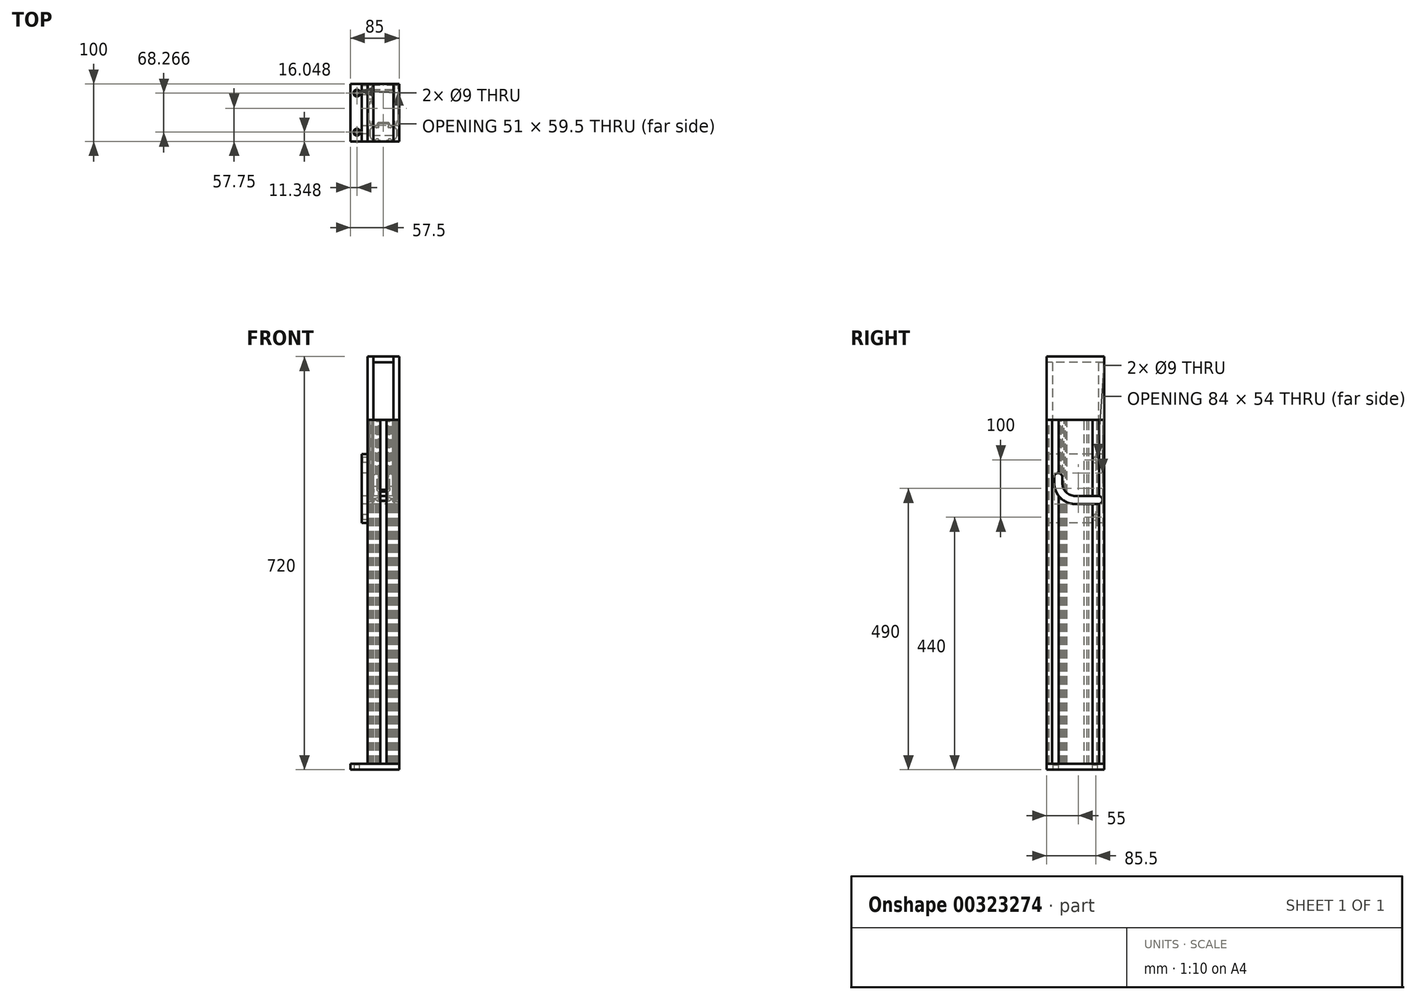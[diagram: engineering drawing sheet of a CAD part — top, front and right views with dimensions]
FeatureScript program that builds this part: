
annotation { "Feature Type Name" : "Feature", "Feature Type Description" : "" }
export const myFeature = defineFeature(function(context is Context, id is Id, definition is map)
    precondition{}
    {
        {
            var Q0;
            Q0=qCreatedBy(makeId("Top.planeOp"),FACE);
            var sketch = newSketch(context, id + "F0", { "sketchPlane" : qUnion([Q0])});
            skArc(sketch, "E0.0.0", {"start": v(6.5, -48) * mm, "mid": v(5.5, -49) * mm, "end": v(6.5, -50) * mm});
            skLineSegment(sketch, "E0.0.1", {"start": v(6.5, -50) * mm, "end": v(25.5, -50) * mm});
            skArc(sketch, "E0.0.2", {"start": v(25.5, -50) * mm, "mid": v(26.91, -49.41) * mm, "end": v(27.5, -48) * mm});
            skLineSegment(sketch, "E0.0.3", {"start": v(27.5, -48) * mm, "end": v(27.5, -41.5) * mm});
            skArc(sketch, "E0.0.4", {"start": v(27.5, -41.5) * mm, "mid": v(27.2, -40.8) * mm, "end": v(26.5, -40.5) * mm});
            skLineSegment(sketch, "E0.0.5", {"start": v(26.5, -40.5) * mm, "end": v(25.3, -40.5) * mm});
            skArc(sketch, "E0.0.6", {"start": v(25.3, -40.5) * mm, "mid": v(24.96, -40.35) * mm, "end": v(24.8, -40) * mm});
            skLineSegment(sketch, "E0.0.7", {"start": v(24.8, -40) * mm, "end": v(24.8, -30) * mm});
            skArc(sketch, "E0.0.8", {"start": v(24.8, -30) * mm, "mid": v(24.96, -29.65) * mm, "end": v(25.3, -29.5) * mm});
            skLineSegment(sketch, "E0.0.9", {"start": v(25.3, -29.5) * mm, "end": v(26.5, -29.5) * mm});
            skArc(sketch, "E0.0.10", {"start": v(26.5, -29.5) * mm, "mid": v(27.2, -29.2) * mm, "end": v(27.5, -28.5) * mm});
            skLineSegment(sketch, "E0.0.11", {"start": v(27.5, -28.5) * mm, "end": v(27.5, 29) * mm});
            skArc(sketch, "E0.0.12", {"start": v(27.5, 29) * mm, "mid": v(26.5, 30) * mm, "end": v(25.5, 29) * mm});
            skLineSegment(sketch, "E0.0.13", {"start": v(25.5, 29) * mm, "end": v(25.5, 24) * mm});
            skArc(sketch, "E0.0.14", {"start": v(25.5, 24) * mm, "mid": v(25.35, 23.65) * mm, "end": v(25, 23.5) * mm});
            skLineSegment(sketch, "E0.0.15", {"start": v(25, 23.5) * mm, "end": v(20.5, 23.5) * mm});
            skArc(sketch, "E0.0.16", {"start": v(20.5, 23.5) * mm, "mid": v(20.15, 23.65) * mm, "end": v(20, 24) * mm});
            skLineSegment(sketch, "E0.0.17", {"start": v(20, 24) * mm, "end": v(20, 47.5) * mm});
            skArc(sketch, "E0.0.18", {"start": v(20, 47.5) * mm, "mid": v(20.15, 47.85) * mm, "end": v(20.5, 48) * mm});
            skLineSegment(sketch, "E0.0.19", {"start": v(20.5, 48) * mm, "end": v(25, 48) * mm});
            skArc(sketch, "E0.0.20", {"start": v(25, 48) * mm, "mid": v(25.35, 47.85) * mm, "end": v(25.5, 47.5) * mm});
            skLineSegment(sketch, "E0.0.21", {"start": v(25.5, 47.5) * mm, "end": v(25.5, 42) * mm});
            skArc(sketch, "E0.0.22", {"start": v(25.5, 42) * mm, "mid": v(26.5, 41) * mm, "end": v(27.5, 42) * mm});
            skLineSegment(sketch, "E0.0.23", {"start": v(27.5, 42) * mm, "end": v(27.5, 48) * mm});
            skArc(sketch, "E0.0.24", {"start": v(27.5, 48) * mm, "mid": v(26.91, 49.41) * mm, "end": v(25.5, 50) * mm});
            skLineSegment(sketch, "E0.0.25", {"start": v(25.5, 50) * mm, "end": v(7, 50) * mm});
            skArc(sketch, "E0.0.26", {"start": v(7, 50) * mm, "mid": v(6, 49) * mm, "end": v(7, 48) * mm});
            skLineSegment(sketch, "E0.0.27", {"start": v(7, 48) * mm, "end": v(17.5, 48) * mm});
            skArc(sketch, "E0.0.28", {"start": v(17.5, 48) * mm, "mid": v(17.85, 47.85) * mm, "end": v(18, 47.5) * mm});
            skLineSegment(sketch, "E0.0.29", {"start": v(18, 47.5) * mm, "end": v(18, 40.5) * mm});
            skArc(sketch, "E0.0.30", {"start": v(18, 40.5) * mm, "mid": v(17.85, 40.15) * mm, "end": v(17.5, 40) * mm});
            skLineSegment(sketch, "E0.0.31", {"start": v(17.5, 40) * mm, "end": v(-17.5, 40) * mm});
            skArc(sketch, "E0.0.32", {"start": v(-17.5, 40) * mm, "mid": v(-17.85, 40.15) * mm, "end": v(-18, 40.5) * mm});
            skLineSegment(sketch, "E0.0.33", {"start": v(-18, 40.5) * mm, "end": v(-18, 47.5) * mm});
            skArc(sketch, "E0.0.34", {"start": v(-18, 47.5) * mm, "mid": v(-17.85, 47.85) * mm, "end": v(-17.5, 48) * mm});
            skLineSegment(sketch, "E0.0.35", {"start": v(-17.5, 48) * mm, "end": v(-7, 48) * mm});
            skArc(sketch, "E0.0.36", {"start": v(-7, 48) * mm, "mid": v(-6, 49) * mm, "end": v(-7, 50) * mm});
            skLineSegment(sketch, "E0.0.37", {"start": v(-7, 50) * mm, "end": v(-25.5, 50) * mm});
            skArc(sketch, "E0.0.38", {"start": v(-25.5, 50) * mm, "mid": v(-26.91, 49.41) * mm, "end": v(-27.5, 48) * mm});
            skLineSegment(sketch, "E0.0.39", {"start": v(-27.5, 48) * mm, "end": v(-27.5, 42) * mm});
            skArc(sketch, "E0.0.40", {"start": v(-27.5, 42) * mm, "mid": v(-26.5, 41) * mm, "end": v(-25.5, 42) * mm});
            skLineSegment(sketch, "E0.0.41", {"start": v(-25.5, 42) * mm, "end": v(-25.5, 47.5) * mm});
            skArc(sketch, "E0.0.42", {"start": v(-25.5, 47.5) * mm, "mid": v(-25.35, 47.85) * mm, "end": v(-25, 48) * mm});
            skLineSegment(sketch, "E0.0.43", {"start": v(-25, 48) * mm, "end": v(-20.5, 48) * mm});
            skArc(sketch, "E0.0.44", {"start": v(-20.5, 48) * mm, "mid": v(-20.15, 47.85) * mm, "end": v(-20, 47.5) * mm});
            skLineSegment(sketch, "E0.0.45", {"start": v(-20, 47.5) * mm, "end": v(-20, 24) * mm});
            skArc(sketch, "E0.0.46", {"start": v(-20, 24) * mm, "mid": v(-20.15, 23.65) * mm, "end": v(-20.5, 23.5) * mm});
            skLineSegment(sketch, "E0.0.47", {"start": v(-20.5, 23.5) * mm, "end": v(-25, 23.5) * mm});
            skArc(sketch, "E0.0.48", {"start": v(-25, 23.5) * mm, "mid": v(-25.35, 23.65) * mm, "end": v(-25.5, 24) * mm});
            skLineSegment(sketch, "E0.0.49", {"start": v(-25.5, 24) * mm, "end": v(-25.5, 29) * mm});
            skArc(sketch, "E0.0.50", {"start": v(-25.5, 29) * mm, "mid": v(-26.5, 30) * mm, "end": v(-27.5, 29) * mm});
            skLineSegment(sketch, "E0.0.51", {"start": v(-27.5, 29) * mm, "end": v(-27.5, -28.5) * mm});
            skArc(sketch, "E0.0.52", {"start": v(-27.5, -28.5) * mm, "mid": v(-27.2, -29.2) * mm, "end": v(-26.5, -29.5) * mm});
            skLineSegment(sketch, "E0.0.53", {"start": v(-26.5, -29.5) * mm, "end": v(-25.3, -29.5) * mm});
            skArc(sketch, "E0.0.54", {"start": v(-25.3, -29.5) * mm, "mid": v(-24.96, -29.65) * mm, "end": v(-24.8, -30) * mm});
            skLineSegment(sketch, "E0.0.55", {"start": v(-24.8, -30) * mm, "end": v(-24.8, -40) * mm});
            skArc(sketch, "E0.0.56", {"start": v(-24.8, -40) * mm, "mid": v(-24.96, -40.35) * mm, "end": v(-25.3, -40.5) * mm});
            skLineSegment(sketch, "E0.0.57", {"start": v(-25.3, -40.5) * mm, "end": v(-26.5, -40.5) * mm});
            skArc(sketch, "E0.0.58", {"start": v(-26.5, -40.5) * mm, "mid": v(-27.2, -40.8) * mm, "end": v(-27.5, -41.5) * mm});
            skLineSegment(sketch, "E0.0.59", {"start": v(-27.5, -41.5) * mm, "end": v(-27.5, -48) * mm});
            skArc(sketch, "E0.0.60", {"start": v(-27.5, -48) * mm, "mid": v(-26.91, -49.41) * mm, "end": v(-25.5, -50) * mm});
            skLineSegment(sketch, "E0.0.61", {"start": v(-25.5, -50) * mm, "end": v(-6.5, -50) * mm});
            skArc(sketch, "E0.0.62", {"start": v(-6.5, -50) * mm, "mid": v(-5.5, -49) * mm, "end": v(-6.5, -48) * mm});
            skLineSegment(sketch, "E0.0.63", {"start": v(-6.5, -48) * mm, "end": v(-8.34, -48) * mm});
            skArc(sketch, "E0.0.64", {"start": v(-8.34, -48) * mm, "mid": v(-8.7, -47.85) * mm, "end": v(-8.84, -47.5) * mm});
            skLineSegment(sketch, "E0.0.65", {"start": v(-8.84, -47.5) * mm, "end": v(-8.84, -46) * mm});
            skArc(sketch, "E0.0.66", {"start": v(-8.84, -46) * mm, "mid": v(-8.98, -45.65) * mm, "end": v(-9.34, -45.5) * mm});
            skLineSegment(sketch, "E0.0.67", {"start": v(-9.34, -45.5) * mm, "end": v(-11.8, -45.5) * mm});
            skArc(sketch, "E0.0.68", {"start": v(-11.8, -45.5) * mm, "mid": v(-12, -45.54) * mm, "end": v(-12.17, -45.65) * mm});
            skArc(sketch, "E0.0.69", {"start": v(-12.17, -45.65) * mm, "mid": v(-17.99, -47.31) * mm, "end": v(-22.3, -43.07) * mm});
            skArc(sketch, "E0.0.70", {"start": v(-22.3, -43.07) * mm, "mid": v(-22.3, -43) * mm, "end": v(-22.3, -42.94) * mm});
            skLineSegment(sketch, "E0.0.71", {"start": v(-22.3, -42.94) * mm, "end": v(-22.3, -29.06) * mm});
            skArc(sketch, "E0.0.72", {"start": v(-22.3, -29.06) * mm, "mid": v(-22.3, -29) * mm, "end": v(-22.3, -28.93) * mm});
            skArc(sketch, "E0.0.73", {"start": v(-22.3, -28.93) * mm, "mid": v(-18.81, -24.96) * mm, "end": v(-13.54, -25.28) * mm});
            skArc(sketch, "E0.0.74", {"start": v(-13.54, -25.28) * mm, "mid": v(-12.42, -26.04) * mm, "end": v(-11.1, -26.31) * mm});
            skLineSegment(sketch, "E0.0.75", {"start": v(-11.1, -26.31) * mm, "end": v(-9.34, -26.31) * mm});
            skArc(sketch, "E0.0.76", {"start": v(-9.34, -26.31) * mm, "mid": v(-8.98, -26.17) * mm, "end": v(-8.84, -25.81) * mm});
            skLineSegment(sketch, "E0.0.77", {"start": v(-8.84, -25.81) * mm, "end": v(-8.84, -21.1) * mm});
            skArc(sketch, "E0.0.78", {"start": v(-8.84, -21.1) * mm, "mid": v(-8.37, -19.97) * mm, "end": v(-7.24, -19.5) * mm});
            skLineSegment(sketch, "E0.0.79", {"start": v(-7.24, -19.5) * mm, "end": v(7.24, -19.5) * mm});
            skArc(sketch, "E0.0.80", {"start": v(7.24, -19.5) * mm, "mid": v(8.37, -19.97) * mm, "end": v(8.84, -21.1) * mm});
            skLineSegment(sketch, "E0.0.81", {"start": v(8.84, -21.1) * mm, "end": v(8.84, -25.81) * mm});
            skArc(sketch, "E0.0.82", {"start": v(8.84, -25.81) * mm, "mid": v(8.98, -26.17) * mm, "end": v(9.34, -26.31) * mm});
            skLineSegment(sketch, "E0.0.83", {"start": v(9.34, -26.31) * mm, "end": v(11.1, -26.31) * mm});
            skArc(sketch, "E0.0.84", {"start": v(11.1, -26.31) * mm, "mid": v(12.42, -26.04) * mm, "end": v(13.54, -25.28) * mm});
            skArc(sketch, "E0.0.85", {"start": v(13.54, -25.28) * mm, "mid": v(18.81, -24.96) * mm, "end": v(22.3, -28.93) * mm});
            skArc(sketch, "E0.0.86", {"start": v(22.3, -28.93) * mm, "mid": v(22.3, -29) * mm, "end": v(22.3, -29.06) * mm});
            skLineSegment(sketch, "E0.0.87", {"start": v(22.3, -29.06) * mm, "end": v(22.3, -42.94) * mm});
            skArc(sketch, "E0.0.88", {"start": v(22.3, -42.94) * mm, "mid": v(22.3, -43) * mm, "end": v(22.3, -43.07) * mm});
            skArc(sketch, "E0.0.89", {"start": v(22.3, -43.07) * mm, "mid": v(17.99, -47.31) * mm, "end": v(12.17, -45.65) * mm});
            skArc(sketch, "E0.0.90", {"start": v(12.17, -45.65) * mm, "mid": v(12, -45.54) * mm, "end": v(11.8, -45.5) * mm});
            skLineSegment(sketch, "E0.0.91", {"start": v(11.8, -45.5) * mm, "end": v(9.34, -45.5) * mm});
            skArc(sketch, "E0.0.92", {"start": v(9.34, -45.5) * mm, "mid": v(8.98, -45.65) * mm, "end": v(8.84, -46) * mm});
            skLineSegment(sketch, "E0.0.93", {"start": v(8.84, -46) * mm, "end": v(8.84, -47.5) * mm});
            skArc(sketch, "E0.0.94", {"start": v(8.84, -47.5) * mm, "mid": v(8.7, -47.85) * mm, "end": v(8.34, -48) * mm});
            skLineSegment(sketch, "E0.0.95", {"start": v(8.34, -48) * mm, "end": v(6.5, -48) * mm});
            skLineSegment(sketch, "E1.0", {"start": v(25.5, -14.1) * mm, "end": v(25.5, 14.6) * mm});
            skArc(sketch, "E2.0", {"start": v(24.85, 15.09) * mm, "mid": v(22.32, 17.3) * mm, "end": v(21.27, 20.49) * mm});
            skArc(sketch, "E3.0", {"start": v(25.5, 14.6) * mm, "mid": v(25.3, 15.01) * mm, "end": v(24.85, 15.09) * mm});
            skArc(sketch, "E4.0", {"start": v(21.27, 20.49) * mm, "mid": v(19.68, 19.32) * mm, "end": v(19.85, 17.36) * mm});
            skArc(sketch, "E5.0", {"start": v(19.85, 17.36) * mm, "mid": v(19.47, 15.28) * mm, "end": v(17.39, 15.66) * mm});
            skArc(sketch, "E6.0", {"start": v(17.39, 15.66) * mm, "mid": v(16.51, 18.88) * mm, "end": v(17.86, 21.93) * mm});
            skArc(sketch, "E7.0", {"start": v(17.86, 21.93) * mm, "mid": v(17.96, 22.1) * mm, "end": v(18, 22.28) * mm});
            skLineSegment(sketch, "E8.0", {"start": v(18, 22.28) * mm, "end": v(18, 36.5) * mm});
            skLineSegment(sketch, "E9.0", {"start": v(17, 37.5) * mm, "end": v(-17, 37.5) * mm});
            skArc(sketch, "E10.0", {"start": v(18, 36.5) * mm, "mid": v(17.7, 37.2) * mm, "end": v(17, 37.5) * mm});
            skArc(sketch, "E11.0", {"start": v(24.85, -14.59) * mm, "mid": v(25.3, -14.51) * mm, "end": v(25.5, -14.1) * mm});
            skArc(sketch, "E12.0", {"start": v(23.15, -16.86) * mm, "mid": v(23.18, -15.11) * mm, "end": v(24.85, -14.59) * mm});
            skArc(sketch, "E13.0", {"start": v(19.85, -16.86) * mm, "mid": v(21.5, -20) * mm, "end": v(23.15, -16.86) * mm});
            skArc(sketch, "E14.0", {"start": v(17.39, -15.16) * mm, "mid": v(19.47, -14.78) * mm, "end": v(19.85, -16.86) * mm});
            skArc(sketch, "E15.0", {"start": v(17.64, -21.18) * mm, "mid": v(16.5, -18.21) * mm, "end": v(17.39, -15.16) * mm});
            skArc(sketch, "E16.0", {"start": v(17.26, -22) * mm, "mid": v(17.7, -21.71) * mm, "end": v(17.64, -21.18) * mm});
            skLineSegment(sketch, "E17.0", {"start": v(11.84, -22) * mm, "end": v(17.26, -22) * mm});
            skArc(sketch, "E18.0", {"start": v(11.34, -21.5) * mm, "mid": v(11.48, -21.85) * mm, "end": v(11.84, -22) * mm});
            skLineSegment(sketch, "E19.0", {"start": v(11.34, -21.1) * mm, "end": v(11.34, -21.5) * mm});
            skArc(sketch, "E20.0", {"start": v(7.24, -17) * mm, "mid": v(10.14, -18.2) * mm, "end": v(11.34, -21.1) * mm});
            skLineSegment(sketch, "E21.0", {"start": v(-7.24, -17) * mm, "end": v(7.24, -17) * mm});
            skArc(sketch, "E22.0", {"start": v(-11.34, -21.1) * mm, "mid": v(-10.14, -18.2) * mm, "end": v(-7.24, -17) * mm});
            skLineSegment(sketch, "E23.0", {"start": v(-11.34, -21.5) * mm, "end": v(-11.34, -21.1) * mm});
            skArc(sketch, "E24.0", {"start": v(-11.84, -22) * mm, "mid": v(-11.48, -21.85) * mm, "end": v(-11.34, -21.5) * mm});
            skLineSegment(sketch, "E25.0", {"start": v(-17.26, -22) * mm, "end": v(-11.84, -22) * mm});
            skArc(sketch, "E26.0", {"start": v(-17.64, -21.18) * mm, "mid": v(-17.7, -21.71) * mm, "end": v(-17.26, -22) * mm});
            skArc(sketch, "E27.0", {"start": v(-17.39, -15.16) * mm, "mid": v(-16.5, -18.21) * mm, "end": v(-17.64, -21.18) * mm});
            skArc(sketch, "E28.0", {"start": v(-19.85, -16.86) * mm, "mid": v(-19.47, -14.78) * mm, "end": v(-17.39, -15.16) * mm});
            skArc(sketch, "E29.0", {"start": v(-23.15, -16.86) * mm, "mid": v(-21.5, -20) * mm, "end": v(-19.85, -16.86) * mm});
            skArc(sketch, "E30.0", {"start": v(-24.85, -14.59) * mm, "mid": v(-23.18, -15.11) * mm, "end": v(-23.15, -16.86) * mm});
            skArc(sketch, "E31.0", {"start": v(-25.5, -14.1) * mm, "mid": v(-25.3, -14.51) * mm, "end": v(-24.85, -14.59) * mm});
            skLineSegment(sketch, "E32.0", {"start": v(-25.5, 14.6) * mm, "end": v(-25.5, -14.1) * mm});
            skArc(sketch, "E33.0", {"start": v(-24.85, 15.09) * mm, "mid": v(-25.3, 15.01) * mm, "end": v(-25.5, 14.6) * mm});
            skArc(sketch, "E34.0", {"start": v(-23.15, 17.36) * mm, "mid": v(-23.18, 15.61) * mm, "end": v(-24.85, 15.09) * mm});
            skArc(sketch, "E35.0", {"start": v(-19.85, 17.36) * mm, "mid": v(-21.5, 20.5) * mm, "end": v(-23.15, 17.36) * mm});
            skArc(sketch, "E36.0", {"start": v(-17.39, 15.66) * mm, "mid": v(-19.47, 15.28) * mm, "end": v(-19.85, 17.36) * mm});
            skArc(sketch, "E37.0", {"start": v(-17.86, 21.93) * mm, "mid": v(-16.51, 18.88) * mm, "end": v(-17.39, 15.66) * mm});
            skArc(sketch, "E38.0", {"start": v(-18, 22.28) * mm, "mid": v(-17.96, 22.1) * mm, "end": v(-17.86, 21.93) * mm});
            skLineSegment(sketch, "E39.0", {"start": v(-18, 36.5) * mm, "end": v(-18, 22.28) * mm});
            skArc(sketch, "E40.0", {"start": v(-17, 37.5) * mm, "mid": v(-17.7, 37.2) * mm, "end": v(-18, 36.5) * mm});
            skLineSegment(sketch, "E41", {"start": v(-7, 50) * mm, "end": v(7, 50) * mm, "construction": true});
            skLineSegment(sketch, "E42", {"start": v(-6.5, -50) * mm, "end": v(6.5, -50) * mm, "construction": true});
            skLineSegment(sketch, "E43", {"start": v(0, -50) * mm, "end": v(0, 50) * mm, "construction": true});
            skLineSegment(sketch, "E44", {"start": v(38.39, 0) * mm, "end": v(-38.32, 0) * mm, "construction": true});
            skPoint(sketch, "E44.startSnap0", {"position": v(0, 0) * mm});
            skSolve(sketch);
        }
        {
            var Q0;
            Q0=makeQuery(id+"F0.imprint","IMPRINT",FACE,{"disambiguationData":[TD([[makeQuery(id+"F0.imprint","IMPRINT",EDGE,{"derivedFrom":sQuery(id+"F0.wireOp",EDGE,"E0.0.0")}),1.0]])]});
            extrude(context, id + "F1", {"entities" : qUnion([Q0]), "oppositeDirection" : true, "depth" : 600 * mm});
        }
        {
            var Q0;
            Q0=makeQuery(id+"F1.opExtrude","SWEPT_FACE",FACE,{"disambiguationData":[OSD([sQuery(id+"F0.wireOp",EDGE,"E0.0.11")])]});
            var sketch = newSketch(context, id + "F2", { "sketchPlane" : qUnion([Q0])});
            skLineSegment(sketch, "E45.bottom", {"start": v(-50, 110) * mm, "end": v(50, 110) * mm});
            skLineSegment(sketch, "E45.top", {"start": v(-50, 0) * mm, "end": v(50, 0) * mm});
            skLineSegment(sketch, "E45.left", {"start": v(-50, 110) * mm, "end": v(-50, 0) * mm});
            skLineSegment(sketch, "E45.right", {"start": v(50, 110) * mm, "end": v(50, 0) * mm});
            skSolve(sketch);
        }
        {
            var Q0;
            Q0 = qSketchRegion(id + "F2", true);
            extrude(context, id + "F3", {"entities" : qUnion([Q0]), "oppositeDirection" : true, "depth" : 10 * mm});
        }
        {
            var Q0;
            Q0=makeQuery(id+"F1.opExtrude","SWEPT_FACE",FACE,{"disambiguationData":[OSD([sQuery(id+"F0.wireOp",EDGE,"E0.0.51")])]});
            var sketch = newSketch(context, id + "F4", { "sketchPlane" : qUnion([Q0])});
            skLineSegment(sketch, "E46.0.0", {"start": v(50, 0) * mm, "end": v(50, 110) * mm});
            skLineSegment(sketch, "E46.0.1", {"start": v(50, 110) * mm, "end": v(-50, 110) * mm});
            skLineSegment(sketch, "E46.0.2", {"start": v(-50, 110) * mm, "end": v(-50, 0) * mm});
            skLineSegment(sketch, "E46.0.3", {"start": v(-50, 0) * mm, "end": v(50, 0) * mm});
            skSolve(sketch);
        }
        {
            var Q0;
            Q0 = qSketchRegion(id + "F4", true);
            extrude(context, id + "F5", {"entities" : qUnion([Q0]), "oppositeDirection" : true, "depth" : 10 * mm});
        }
        {
            var Q0;
            Q0=makeQuery(id+"F3.opExtrude","CAP_FACE",FACE,{"disambiguationData":[OSD([sQuery(id+"F2.wireOp",EDGE,"E45.bottom"),sQuery(id+"F2.wireOp",EDGE,"E45.top"),sQuery(id+"F2.wireOp",EDGE,"E45.left"),sQuery(id+"F2.wireOp",EDGE,"E45.right")])],"isStart":false});
            var sketch = newSketch(context, id + "F6", { "sketchPlane" : qUnion([Q0])});
            skLineSegment(sketch, "E47.bottom", {"start": v(-50, 110) * mm, "end": v(50, 110) * mm});
            skLineSegment(sketch, "E47.top", {"start": v(-50, 100) * mm, "end": v(50, 100) * mm});
            skLineSegment(sketch, "E47.left", {"start": v(-50, 110) * mm, "end": v(-50, 100) * mm});
            skLineSegment(sketch, "E47.right", {"start": v(50, 110) * mm, "end": v(50, 100) * mm});
            skSolve(sketch);
        }
        {
            var Q0;
            Q0 = qSketchRegion(id + "F6", true);
            extrude(context, id + "F7", {"entities" : qUnion([Q0]), "endBound" : BoundingType.UP_TO_NEXT, "depth" : 25 * mm});
        }
        {
            var Q0;
            Q0=makeQuery(id+"F3.opExtrude","SWEPT_FACE",FACE,{"disambiguationData":[OSD([sQuery(id+"F2.wireOp",EDGE,"E45.left")])]});
            var sketch = newSketch(context, id + "F8", { "sketchPlane" : qUnion([Q0])});
            skLineSegment(sketch, "E48.bottom", {"start": v(17.5, 0) * mm, "end": v(-17.5, 0) * mm});
            skLineSegment(sketch, "E48.top", {"start": v(17.5, 100) * mm, "end": v(-17.5, 100) * mm});
            skLineSegment(sketch, "E48.left", {"start": v(17.5, 0) * mm, "end": v(17.5, 100) * mm});
            skLineSegment(sketch, "E48.right", {"start": v(-17.5, 0) * mm, "end": v(-17.5, 100) * mm});
            skSolve(sketch);
        }
        {
            var Q0;
            Q0 = qSketchRegion(id + "F8", true);
            extrude(context, id + "F9", {"entities" : qUnion([Q0]), "oppositeDirection" : true, "depth" : 10 * mm});
        }
        {
            var Q0;
            Q0=makeQuery(id+"F3.opExtrude","SWEPT_FACE",FACE,{"disambiguationData":[OSD([sQuery(id+"F2.wireOp",EDGE,"E45.right")])]});
            var sketch = newSketch(context, id + "F10", { "sketchPlane" : qUnion([Q0])});
            skLineSegment(sketch, "E49.0.0", {"start": v(-17.5, 0) * mm, "end": v(-17.5, 100) * mm});
            skLineSegment(sketch, "E49.0.1", {"start": v(-17.5, 100) * mm, "end": v(17.5, 100) * mm});
            skLineSegment(sketch, "E49.0.2", {"start": v(17.5, 100) * mm, "end": v(17.5, 0) * mm});
            skLineSegment(sketch, "E49.0.3", {"start": v(17.5, 0) * mm, "end": v(-17.5, 0) * mm});
            skSolve(sketch);
        }
        {
            var Q0;
            Q0 = qSketchRegion(id + "F10", true);
            extrude(context, id + "F11", {"entities" : qUnion([Q0]), "oppositeDirection" : true, "depth" : 10 * mm});
        }
        {
            var Q0;
            Q0=makeQuery(id+"F1.opExtrude","CAP_FACE",FACE,{"disambiguationData":[OSD([sQuery(id+"F0.wireOp",EDGE,"E0.0.0"),sQuery(id+"F0.wireOp",EDGE,"E0.0.1"),sQuery(id+"F0.wireOp",EDGE,"E0.0.2"),sQuery(id+"F0.wireOp",EDGE,"E0.0.3"),sQuery(id+"F0.wireOp",EDGE,"E0.0.4"),sQuery(id+"F0.wireOp",EDGE,"E0.0.5"),sQuery(id+"F0.wireOp",EDGE,"E0.0.6"),sQuery(id+"F0.wireOp",EDGE,"E0.0.7"),sQuery(id+"F0.wireOp",EDGE,"E0.0.8"),sQuery(id+"F0.wireOp",EDGE,"E0.0.9"),sQuery(id+"F0.wireOp",EDGE,"E0.0.10"),sQuery(id+"F0.wireOp",EDGE,"E0.0.11"),sQuery(id+"F0.wireOp",EDGE,"E0.0.12"),sQuery(id+"F0.wireOp",EDGE,"E0.0.13"),sQuery(id+"F0.wireOp",EDGE,"E0.0.14"),sQuery(id+"F0.wireOp",EDGE,"E0.0.15"),sQuery(id+"F0.wireOp",EDGE,"E0.0.16"),sQuery(id+"F0.wireOp",EDGE,"E0.0.17"),sQuery(id+"F0.wireOp",EDGE,"E0.0.18"),sQuery(id+"F0.wireOp",EDGE,"E0.0.19"),sQuery(id+"F0.wireOp",EDGE,"E0.0.20"),sQuery(id+"F0.wireOp",EDGE,"E0.0.21"),sQuery(id+"F0.wireOp",EDGE,"E0.0.22"),sQuery(id+"F0.wireOp",EDGE,"E0.0.23"),sQuery(id+"F0.wireOp",EDGE,"E0.0.24"),sQuery(id+"F0.wireOp",EDGE,"E0.0.25"),sQuery(id+"F0.wireOp",EDGE,"E0.0.26"),sQuery(id+"F0.wireOp",EDGE,"E0.0.27"),sQuery(id+"F0.wireOp",EDGE,"E0.0.28"),sQuery(id+"F0.wireOp",EDGE,"E0.0.29"),sQuery(id+"F0.wireOp",EDGE,"E0.0.30"),sQuery(id+"F0.wireOp",EDGE,"E0.0.31"),sQuery(id+"F0.wireOp",EDGE,"E0.0.32"),sQuery(id+"F0.wireOp",EDGE,"E0.0.33"),sQuery(id+"F0.wireOp",EDGE,"E0.0.34"),sQuery(id+"F0.wireOp",EDGE,"E0.0.35"),sQuery(id+"F0.wireOp",EDGE,"E0.0.36"),sQuery(id+"F0.wireOp",EDGE,"E0.0.37"),sQuery(id+"F0.wireOp",EDGE,"E0.0.38"),sQuery(id+"F0.wireOp",EDGE,"E0.0.39"),sQuery(id+"F0.wireOp",EDGE,"E0.0.40"),sQuery(id+"F0.wireOp",EDGE,"E0.0.41"),sQuery(id+"F0.wireOp",EDGE,"E0.0.42"),sQuery(id+"F0.wireOp",EDGE,"E0.0.43"),sQuery(id+"F0.wireOp",EDGE,"E0.0.44"),sQuery(id+"F0.wireOp",EDGE,"E0.0.45"),sQuery(id+"F0.wireOp",EDGE,"E0.0.46"),sQuery(id+"F0.wireOp",EDGE,"E0.0.47"),sQuery(id+"F0.wireOp",EDGE,"E0.0.48"),sQuery(id+"F0.wireOp",EDGE,"E0.0.49"),sQuery(id+"F0.wireOp",EDGE,"E0.0.50"),sQuery(id+"F0.wireOp",EDGE,"E0.0.51"),sQuery(id+"F0.wireOp",EDGE,"E0.0.52"),sQuery(id+"F0.wireOp",EDGE,"E0.0.53"),sQuery(id+"F0.wireOp",EDGE,"E0.0.54"),sQuery(id+"F0.wireOp",EDGE,"E0.0.55"),sQuery(id+"F0.wireOp",EDGE,"E0.0.56"),sQuery(id+"F0.wireOp",EDGE,"E0.0.57"),sQuery(id+"F0.wireOp",EDGE,"E0.0.58"),sQuery(id+"F0.wireOp",EDGE,"E0.0.59"),sQuery(id+"F0.wireOp",EDGE,"E0.0.60"),sQuery(id+"F0.wireOp",EDGE,"E0.0.61"),sQuery(id+"F0.wireOp",EDGE,"E0.0.62"),sQuery(id+"F0.wireOp",EDGE,"E0.0.63"),sQuery(id+"F0.wireOp",EDGE,"E0.0.64"),sQuery(id+"F0.wireOp",EDGE,"E0.0.65"),sQuery(id+"F0.wireOp",EDGE,"E0.0.66"),sQuery(id+"F0.wireOp",EDGE,"E0.0.67"),sQuery(id+"F0.wireOp",EDGE,"E0.0.68"),sQuery(id+"F0.wireOp",EDGE,"E0.0.69"),sQuery(id+"F0.wireOp",EDGE,"E0.0.70"),sQuery(id+"F0.wireOp",EDGE,"E0.0.71"),sQuery(id+"F0.wireOp",EDGE,"E0.0.72"),sQuery(id+"F0.wireOp",EDGE,"E0.0.73"),sQuery(id+"F0.wireOp",EDGE,"E0.0.74"),sQuery(id+"F0.wireOp",EDGE,"E0.0.75"),sQuery(id+"F0.wireOp",EDGE,"E0.0.76"),sQuery(id+"F0.wireOp",EDGE,"E0.0.77"),sQuery(id+"F0.wireOp",EDGE,"E0.0.78"),sQuery(id+"F0.wireOp",EDGE,"E0.0.79"),sQuery(id+"F0.wireOp",EDGE,"E0.0.80"),sQuery(id+"F0.wireOp",EDGE,"E0.0.81"),sQuery(id+"F0.wireOp",EDGE,"E0.0.82"),sQuery(id+"F0.wireOp",EDGE,"E0.0.83"),sQuery(id+"F0.wireOp",EDGE,"E0.0.84"),sQuery(id+"F0.wireOp",EDGE,"E0.0.85"),sQuery(id+"F0.wireOp",EDGE,"E0.0.86"),sQuery(id+"F0.wireOp",EDGE,"E0.0.87"),sQuery(id+"F0.wireOp",EDGE,"E0.0.88"),sQuery(id+"F0.wireOp",EDGE,"E0.0.89"),sQuery(id+"F0.wireOp",EDGE,"E0.0.90"),sQuery(id+"F0.wireOp",EDGE,"E0.0.91"),sQuery(id+"F0.wireOp",EDGE,"E0.0.92"),sQuery(id+"F0.wireOp",EDGE,"E0.0.93"),sQuery(id+"F0.wireOp",EDGE,"E0.0.94"),sQuery(id+"F0.wireOp",EDGE,"E0.0.95"),sQuery(id+"F0.wireOp",EDGE,"E1.0"),sQuery(id+"F0.wireOp",EDGE,"E2.0"),sQuery(id+"F0.wireOp",EDGE,"E3.0"),sQuery(id+"F0.wireOp",EDGE,"E4.0"),sQuery(id+"F0.wireOp",EDGE,"E5.0"),sQuery(id+"F0.wireOp",EDGE,"E6.0"),sQuery(id+"F0.wireOp",EDGE,"E7.0"),sQuery(id+"F0.wireOp",EDGE,"E8.0"),sQuery(id+"F0.wireOp",EDGE,"E9.0"),sQuery(id+"F0.wireOp",EDGE,"E10.0"),sQuery(id+"F0.wireOp",EDGE,"E11.0"),sQuery(id+"F0.wireOp",EDGE,"E12.0"),sQuery(id+"F0.wireOp",EDGE,"E13.0"),sQuery(id+"F0.wireOp",EDGE,"E14.0"),sQuery(id+"F0.wireOp",EDGE,"E15.0"),sQuery(id+"F0.wireOp",EDGE,"E16.0"),sQuery(id+"F0.wireOp",EDGE,"E17.0"),sQuery(id+"F0.wireOp",EDGE,"E18.0"),sQuery(id+"F0.wireOp",EDGE,"E19.0"),sQuery(id+"F0.wireOp",EDGE,"E20.0"),sQuery(id+"F0.wireOp",EDGE,"E21.0"),sQuery(id+"F0.wireOp",EDGE,"E22.0"),sQuery(id+"F0.wireOp",EDGE,"E23.0"),sQuery(id+"F0.wireOp",EDGE,"E24.0"),sQuery(id+"F0.wireOp",EDGE,"E25.0"),sQuery(id+"F0.wireOp",EDGE,"E26.0"),sQuery(id+"F0.wireOp",EDGE,"E27.0"),sQuery(id+"F0.wireOp",EDGE,"E28.0"),sQuery(id+"F0.wireOp",EDGE,"E29.0"),sQuery(id+"F0.wireOp",EDGE,"E30.0"),sQuery(id+"F0.wireOp",EDGE,"E31.0"),sQuery(id+"F0.wireOp",EDGE,"E32.0"),sQuery(id+"F0.wireOp",EDGE,"E33.0"),sQuery(id+"F0.wireOp",EDGE,"E34.0"),sQuery(id+"F0.wireOp",EDGE,"E35.0"),sQuery(id+"F0.wireOp",EDGE,"E36.0"),sQuery(id+"F0.wireOp",EDGE,"E37.0"),sQuery(id+"F0.wireOp",EDGE,"E38.0"),sQuery(id+"F0.wireOp",EDGE,"E39.0"),sQuery(id+"F0.wireOp",EDGE,"E40.0")])],"isStart":false});
            var sketch = newSketch(context, id + "F12", { "sketchPlane" : qUnion([Q0])});
            skLineSegment(sketch, "E50.bottom", {"start": v(27.5, -50) * mm, "end": v(-57.5, -50) * mm});
            skLineSegment(sketch, "E50.top", {"start": v(27.5, 50) * mm, "end": v(-57.5, 50) * mm});
            skLineSegment(sketch, "E50.left", {"start": v(27.5, -50) * mm, "end": v(27.5, 50) * mm});
            skLineSegment(sketch, "E50.right", {"start": v(-57.5, -50) * mm, "end": v(-57.5, 50) * mm});
            skSolve(sketch);
        }
        {
            var Q0;
            Q0 = qSketchRegion(id + "F12", true);
            extrude(context, id + "F13", {"entities" : qUnion([Q0]), "depth" : 10 * mm});
        }
        {
            var Q0;
            Q0=makeQuery(id+"F13.opExtrude","CAP_FACE",FACE,{"disambiguationData":[OSD([sQuery(id+"F12.wireOp",EDGE,"E50.bottom"),sQuery(id+"F12.wireOp",EDGE,"E50.top"),sQuery(id+"F12.wireOp",EDGE,"E50.left"),sQuery(id+"F12.wireOp",EDGE,"E50.right")])],"isStart":true});
            var sketch = newSketch(context, id + "F14", { "sketchPlane" : qUnion([Q0])});
            skPoint(sketch, "E51", {"position": v(-46.15, 34.31) * mm});
            skPoint(sketch, "E52", {"position": v(-46.15, -33.95) * mm});
            skSolve(sketch);
        }
        {
            var Q0;
            Q0=sQuery(id+"F14.wireOp",VERTEX,"E51");
            var Q1;
            Q1=sQuery(id+"F14.wireOp",VERTEX,"E52");
            var Q2;
            Q2=makeQuery(id+"F13.opExtrude","SWEPT_BODY",BODY,{"disambiguationData":[OSD([sQuery(id+"F12.wireOp",EDGE,"E50.bottom"),sQuery(id+"F12.wireOp",EDGE,"E50.top"),sQuery(id+"F12.wireOp",EDGE,"E50.left"),sQuery(id+"F12.wireOp",EDGE,"E50.right")])]});
            hole(context, id + "F15", {"style" : HoleStyle.C_SINK, "endStyle" : HoleEndStyle.THROUGH, "holeDiameter" : 9 * mm, "cSinkDiameter" : 12 * mm, "cSinkAngle" : 90 * degree, "tappedDepth" : 12 * mm, "tapClearance" : 3, "locations" : qUnion([Q0, Q1]), "scope" : qUnion([Q2])});
        }
        {
            var Q0;
            Q0=makeQuery(id+"F1.opExtrude","SWEPT_FACE",FACE,{"disambiguationData":[OSD([sQuery(id+"F0.wireOp",EDGE,"E0.0.51")])]});
            var sketch = newSketch(context, id + "F16", { "sketchPlane" : qUnion([Q0])});
            skLineSegment(sketch, "E53.bottom", {"start": v(-50, -180) * mm, "end": v(50, -180) * mm});
            skLineSegment(sketch, "E53.top", {"start": v(-50, -60) * mm, "end": v(50, -60) * mm});
            skLineSegment(sketch, "E53.left", {"start": v(-50, -180) * mm, "end": v(-50, -60) * mm});
            skLineSegment(sketch, "E53.right", {"start": v(50, -180) * mm, "end": v(50, -60) * mm});
            skSolve(sketch);
        }
        {
            var Q0;
            Q0 = qSketchRegion(id + "F16", true);
            extrude(context, id + "F17", {"entities" : qUnion([Q0]), "depth" : 10 * mm});
        }
        {
            var Q0;
            Q0=makeQuery(id+"F17.opExtrude","CAP_FACE",FACE,{"disambiguationData":[OSD([sQuery(id+"F16.wireOp",EDGE,"E53.bottom"),sQuery(id+"F16.wireOp",EDGE,"E53.top"),sQuery(id+"F16.wireOp",EDGE,"E53.left"),sQuery(id+"F16.wireOp",EDGE,"E53.right")])],"isStart":false});
            var sketch = newSketch(context, id + "F18", { "sketchPlane" : qUnion([Q0])});
            skPoint(sketch, "E54", {"position": v(-35.5, -70) * mm});
            skPoint(sketch, "E55", {"position": v(-35.5, -170) * mm});
            skLineSegment(sketch, "E56", {"start": v(-35.5, -170) * mm, "end": v(-35.5, -70) * mm, "construction": true});
            skLineSegment(sketch, "E57", {"start": v(-35.5, -120) * mm, "end": v(-50, -120) * mm, "construction": true});
            skPoint(sketch, "E57.endSnap0", {"position": v(-50, -120) * mm});
            skSolve(sketch);
        }
        {
            var Q0;
            Q0=sQuery(id+"F18.wireOp",VERTEX,"E54");
            var Q1;
            Q1=sQuery(id+"F18.wireOp",VERTEX,"E55");
            var Q2;
            Q2=makeQuery(id+"F17.opExtrude","SWEPT_BODY",BODY,{"disambiguationData":[OSD([sQuery(id+"F16.wireOp",EDGE,"E53.bottom"),sQuery(id+"F16.wireOp",EDGE,"E53.top"),sQuery(id+"F16.wireOp",EDGE,"E53.left"),sQuery(id+"F16.wireOp",EDGE,"E53.right")])]});
            hole(context, id + "F19", {"style" : HoleStyle.C_SINK, "endStyle" : HoleEndStyle.THROUGH, "holeDiameter" : 9 * mm, "cSinkDiameter" : 11 * mm, "cSinkAngle" : 90 * degree, "tappedDepth" : 12 * mm, "tapClearance" : 3, "locations" : qUnion([Q0, Q1]), "scope" : qUnion([Q2])});
        }
        {
            var Q0;
            Q0=makeQuery(id+"F17.opExtrude","CAP_FACE",FACE,{"disambiguationData":[OSD([sQuery(id+"F16.wireOp",EDGE,"E53.bottom"),sQuery(id+"F16.wireOp",EDGE,"E53.top"),sQuery(id+"F16.wireOp",EDGE,"E53.left"),sQuery(id+"F16.wireOp",EDGE,"E53.right")])],"isStart":false});
            var sketch = newSketch(context, id + "F20", { "sketchPlane" : qUnion([Q0])});
            skLineSegment(sketch, "E58", {"start": v(-40, -140) * mm, "end": v(0, -140) * mm, "construction": true});
            skArc(sketch, "E59", {"start": v(0, -140) * mm, "mid": v(21.21, -131.21) * mm, "end": v(30, -110) * mm, "construction": true});
            skArc(sketch, "E60.0", {"start": v(0, -147) * mm, "mid": v(26.16, -136.16) * mm, "end": v(37, -110) * mm});
            skLineSegment(sketch, "E60.1", {"start": v(-40, -147) * mm, "end": v(0, -147) * mm});
            skArc(sketch, "E61.0", {"start": v(0, -133) * mm, "mid": v(16.26, -126.26) * mm, "end": v(23, -110) * mm});
            skLineSegment(sketch, "E61.1", {"start": v(-40, -133) * mm, "end": v(0, -133) * mm});
            skArc(sketch, "E62", {"start": v(-40, -133) * mm, "mid": v(-47, -140) * mm, "end": v(-40, -147) * mm});
            skLineSegment(sketch, "E63", {"start": v(-40, -140) * mm, "end": v(-50, -140) * mm, "construction": true});
            skLineSegment(sketch, "E64", {"start": v(0, -140) * mm, "end": v(0, -180) * mm, "construction": true});
            skLineSegment(sketch, "E65", {"start": v(30, -110) * mm, "end": v(30, -100) * mm, "construction": true});
            skLineSegment(sketch, "E66", {"start": v(37, -110) * mm, "end": v(37, -100) * mm});
            skArc(sketch, "E67", {"start": v(37, -100) * mm, "mid": v(30, -93) * mm, "end": v(23, -100) * mm});
            skLineSegment(sketch, "E68", {"start": v(23, -110) * mm, "end": v(23, -100) * mm});
            skLineSegment(sketch, "E69.trimOffspring", {"start": v(30, -100) * mm, "end": v(30, -60) * mm, "construction": true});
            skSolve(sketch);
        }
        {
            var Q0;
            Q0 = qSketchRegion(id + "F20", true);
            extrude(context, id + "F21", {"entities" : qUnion([Q0]), "operationType" : NewBodyOperationType.REMOVE, "endBound" : BoundingType.THROUGH_ALL, "oppositeDirection" : true, "depth" : 25 * mm});
        }
    });
